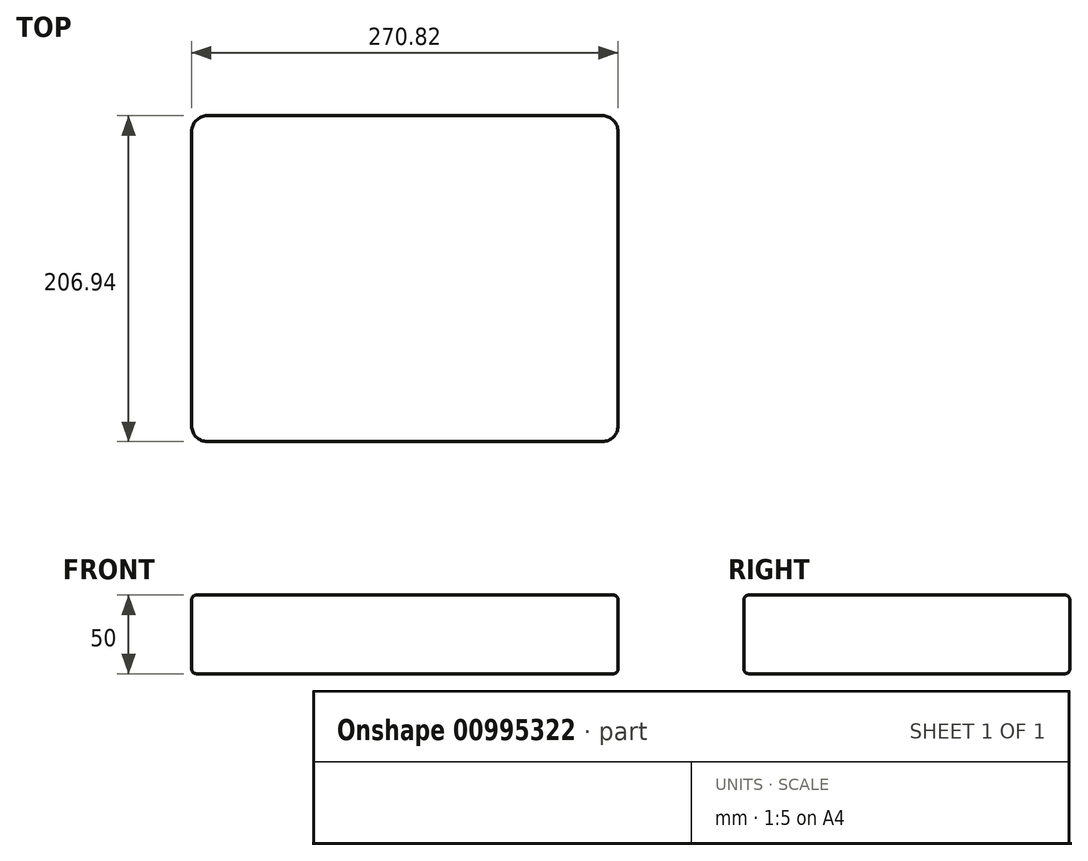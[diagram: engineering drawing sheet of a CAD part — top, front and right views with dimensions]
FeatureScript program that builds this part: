
annotation { "Feature Type Name" : "Feature", "Feature Type Description" : "" }
export const myFeature = defineFeature(function(context is Context, id is Id, definition is map)
    precondition{}
    {
        {
            var Q0;
            Q0=qCreatedBy(makeId("Top.planeOp"),FACE);
            var sketch = newSketch(context, id + "F0", { "sketchPlane" : qUnion([Q0])});
            skLineSegment(sketch, "E0.bottom", {"start": v(-125.4, -103.47) * mm, "end": v(125.4, -103.47) * mm});
            skLineSegment(sketch, "E0.top", {"start": v(-125.4, 103.47) * mm, "end": v(125.4, 103.47) * mm});
            skLineSegment(sketch, "E0.left", {"start": v(-135.4, -93.47) * mm, "end": v(-135.4, 93.47) * mm});
            skLineSegment(sketch, "E0.right", {"start": v(135.4, -93.47) * mm, "end": v(135.4, 93.47) * mm});
            skPoint(sketch, "E0.middle", {"position": v(0, 0) * mm});
            skPoint(sketch, "E1.visualSharp", {"position": v(-135.4, 103.47) * mm});
            skArc(sketch, "E1.filletArc", {"start": v(-125.4, 103.47) * mm, "mid": v(-132.48, 100.54) * mm, "end": v(-135.4, 93.47) * mm});
            skPoint(sketch, "E2.visualSharp", {"position": v(-135.4, -103.47) * mm});
            skArc(sketch, "E2.filletArc", {"start": v(-135.4, -93.47) * mm, "mid": v(-132.48, -100.54) * mm, "end": v(-125.4, -103.47) * mm});
            skPoint(sketch, "E3.visualSharp", {"position": v(135.4, -103.47) * mm});
            skArc(sketch, "E3.filletArc", {"start": v(125.4, -103.47) * mm, "mid": v(132.48, -100.54) * mm, "end": v(135.4, -93.47) * mm});
            skPoint(sketch, "E4.visualSharp", {"position": v(135.4, 103.47) * mm});
            skArc(sketch, "E4.filletArc", {"start": v(135.4, 93.47) * mm, "mid": v(132.48, 100.54) * mm, "end": v(125.4, 103.47) * mm});
            skSolve(sketch);
        }
        {
            var Q0;
            Q0=makeQuery(id+"F0.imprint","IMPRINT",FACE,{"disambiguationData":[TD([[makeQuery(id+"F0.imprint","IMPRINT",EDGE,{"derivedFrom":sQuery(id+"F0.wireOp",EDGE,"E0.bottom")}),1.0]])]});
            extrude(context, id + "F1", {"entities" : qUnion([Q0]), "depth" : 50 * mm, "offsetDistance" : 25 * mm});
        }
        {
            var Q0;
            Q0=makeQuery(id+"F1.opExtrude","CAP_EDGE",EDGE,{"disambiguationData":[OSD([sQuery(id+"F0.wireOp",EDGE,"E0.left")])],"isStart":false});
            var Q1;
            Q1=makeQuery(id+"F1.opExtrude","CAP_EDGE",EDGE,{"disambiguationData":[OSD([sQuery(id+"F0.wireOp",EDGE,"E0.left")])],"isStart":true});
            fillet(context, id + "F2", {"entities" : qUnion([Q0, Q1]), "radius" : 3 * mm, "tangentPropagation" : true, "allowEdgeOverflow" : false});
        }
    });
